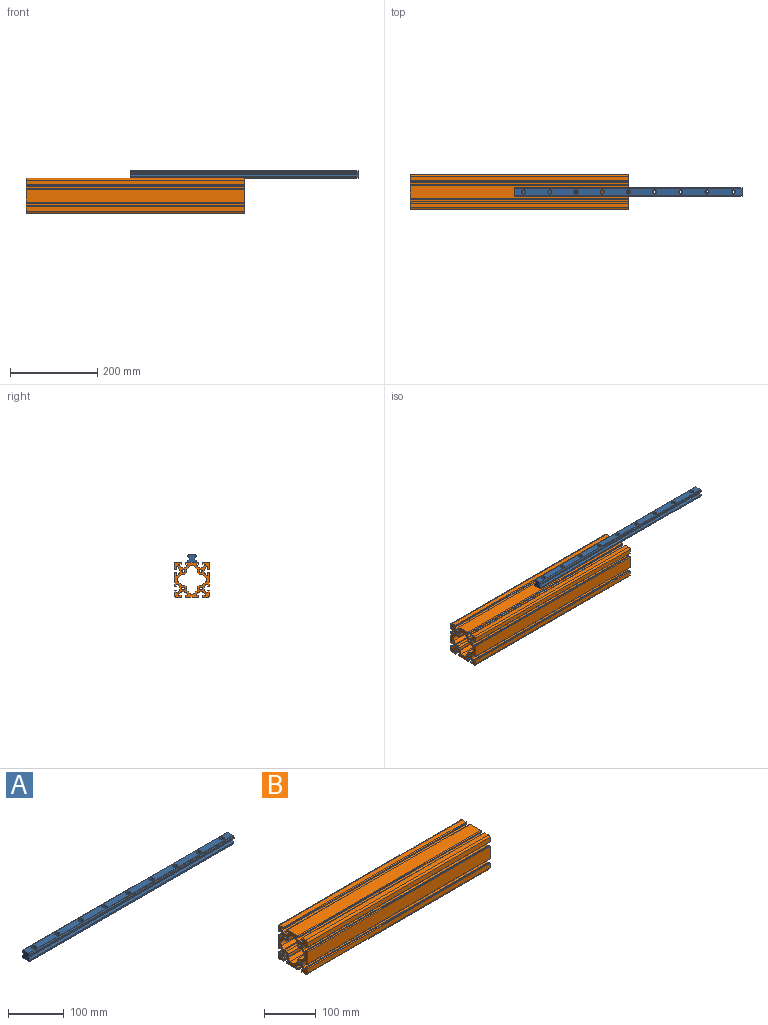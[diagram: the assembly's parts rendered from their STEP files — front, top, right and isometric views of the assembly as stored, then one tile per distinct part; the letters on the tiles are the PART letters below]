
ASSEMBLY  parts=2 mates=1
PART A: 53 faces, bbox 520x20x17.4 mm
  f0: cylinder r=3mm len=9mm, axis (0,0,1), area 169.6mm2, adj f27,f29
  f1: cylinder r=3mm len=9mm, axis (0,0,1), area 169.6mm2, adj f27,f30
  f2: cylinder r=3mm len=9mm, axis (0,0,1), area 169.6mm2, adj f27,f31
  f3: cylinder r=3mm len=9mm, axis (0,0,1), area 169.6mm2, adj f27,f32
  f4: cylinder r=3mm len=9mm, axis (0,0,1), area 169.6mm2, adj f27,f33
  f5: cylinder r=3mm len=9mm, axis (0,0,1), area 169.6mm2, adj f27,f34
  f6: cylinder r=3mm len=9mm, axis (0,0,1), area 169.6mm2, adj f27,f35
  f7: cylinder r=3mm len=9mm, axis (0,0,-1), area 169.6mm2, adj f27,f36
  f8: plane 520x3mm, normal (0,-1,0), area 1559.9mm2, adj f9,f28,f39,f41
  f9: plane 520x3.45mm, normal (0,-0.71,0.71), area 2537.2mm2, adj f8,f10,f39,f41
  f10: plane 520x2.43mm, normal (0,-1,0), area 1263.5mm2, adj f9,f11,f39,f41
  f11: plane 520x1.11mm, normal (0,-0.71,-0.71), area 815.2mm2, adj f10,f12,f39,f41
  f12: cylinder r=2.13mm len=520mm, axis (1,0,0), area 1543.6mm2, adj f11,f13,f39,f41
  f13: plane 520x0.41mm, normal (0,-0.71,-0.71), area 300.2mm2, adj f12,f14,f39,f41
  f14: plane 520x1.33mm, normal (0,-1,0), area 691.6mm2, adj f13,f15,f39,f41
  f15: plane 520x0.42mm, normal (0,-0.71,0.71), area 308.2mm2, adj f14,f16,f39,f41
  f16: cylinder r=2.13mm len=520mm, axis (1,0,0), area 1532.3mm2, adj f15,f38,f39,f41
  f17: cylinder r=2.13mm len=520mm, axis (1,0,0), area 1532.3mm2, adj f18,f39,f40,f41
  f18: plane 520x0.42mm, normal (0,0.71,0.71), area 308.1mm2, adj f17,f19,f39,f41
  f19: plane 520x1.33mm, normal (0,1,0), area 692mm2, adj f18,f20,f39,f41
  f20: plane 520x0.41mm, normal (0,0.71,-0.71), area 299.7mm2, adj f19,f21,f39,f41
  f21: cylinder r=2.13mm len=520mm, axis (1,0,0), area 1544.6mm2, adj f20,f22,f39,f41
  f22: plane 520x1.11mm, normal (0,0.71,-0.71), area 815mm2, adj f21,f23,f39,f41
  f23: plane 520x2.43mm, normal (0,1,0), area 1263.2mm2, adj f22,f24,f39,f41
  f24: plane 520x3.45mm, normal (0,0.71,0.71), area 2537.3mm2, adj f23,f25,f39,f41
  f25: plane 520x3mm, normal (0,1,0), area 1559.9mm2, adj f24,f26,f39,f41
  f26: plane 520x1mm, normal (0,0.71,-0.71), area 735.4mm2, adj f25,f27,f39,f41
  f27: plane 520x18mm, normal (0,0,-1), area 9105.5mm2, adj f0,f1,f2,f3,f4,f5,f6,f7
  f28: plane 520x1mm, normal (0,-0.71,-0.71), area 735.4mm2, adj f8,f27,f39,f41
  f29: plane 9.5x9.5mm, normal (0,0,1), area 42.6mm2, adj f0,f42
  f30: plane 9.5x9.5mm, normal (0,0,1), area 42.6mm2, adj f1,f43
  f31: plane 9.5x9.5mm, normal (0,0,1), area 42.6mm2, adj f2,f44
  f32: plane 9.5x9.5mm, normal (0,0,1), area 42.6mm2, adj f3,f45
  f33: plane 9.5x9.5mm, normal (0,0,1), area 42.6mm2, adj f4,f46
  f34: plane 9.5x9.5mm, normal (0,0,1), area 42.6mm2, adj f5,f47
  f35: plane 9.5x9.5mm, normal (0,0,1), area 42.6mm2, adj f6,f48
  f36: plane 9.5x9.5mm, normal (0,0,1), area 42.6mm2, adj f7,f49
  f37: cylinder r=3mm len=9mm, axis (0,0,1), area 169.6mm2, adj f27,f50
  f38: plane 520x0.4mm, normal (0,-0.71,0.71), area 293.8mm2, adj f16,f39,f41,f51
  f39: plane 20x17.4mm, normal (-1,0,0), area 295.2mm2, adj f8,f9,f10,f11,f12,f13,f14,f15
  f40: plane 520x0.4mm, normal (0,0.71,0.71), area 293.8mm2, adj f17,f39,f41,f51
  f41: plane 20x17.4mm, normal (1,0,0), area 295.2mm2, adj f8,f9,f10,f11,f12,f13,f14,f15
  f42: cylinder r=4.75mm len=9.5mm, axis (0,0,1), area 250.7mm2, adj f29,f51
  f43: cylinder r=4.75mm len=9.5mm, axis (0,0,1), area 250.7mm2, adj f30,f51
  f44: cylinder r=4.75mm len=9.5mm, axis (0,0,1), area 250.7mm2, adj f31,f51
  f45: cylinder r=4.75mm len=9.5mm, axis (0,0,1), area 250.7mm2, adj f32,f51
  f46: cylinder r=4.75mm len=9.5mm, axis (0,0,1), area 250.7mm2, adj f33,f51
  f47: cylinder r=4.75mm len=9.5mm, axis (0,0,1), area 250.7mm2, adj f34,f51
  f48: cylinder r=4.75mm len=9.5mm, axis (0,0,1), area 250.7mm2, adj f35,f51
  f49: cylinder r=4.75mm len=9.5mm, axis (0,0,-1), area 250.7mm2, adj f36,f51
  f50: plane 9.5x9.5mm, normal (0,0,1), area 42.6mm2, adj f37,f52
  f51: plane 520x14.52mm, normal (0,0,1), area 6912.5mm2, adj f38,f39,f40,f41,f42,f43,f44,f45
  f52: cylinder r=4.75mm len=9.5mm, axis (0,0,1), area 250.7mm2, adj f50,f51
PART B: 174 faces, bbox 500x80x80 mm
  f0: cylinder r=25mm len=500mm, axis (1,0,0), area 3705.1mm2, adj f1,f169,f172,f173
  f1: cylinder r=4mm len=500mm, axis (1,0,0), area 1279mm2, adj f0,f2,f172,f173
  f2: plane 500x4.39mm, normal (0,-1,0), area 2193.1mm2, adj f1,f3,f172,f173
  f3: cylinder r=4mm len=500mm, axis (1,0,0), area 1279mm2, adj f2,f4,f172,f173
  f4: cylinder r=25mm len=500mm, axis (1,0,0), area 3705.1mm2, adj f3,f5,f172,f173
  f5: cylinder r=1.08mm len=500mm, axis (1,0,0), area 1195.3mm2, adj f4,f6,f172,f173
  f6: plane 500x3.92mm, normal (0,1,0), area 1958.1mm2, adj f5,f7,f172,f173
  f7: cylinder r=1mm len=500mm, axis (1,0,0), area 785.4mm2, adj f6,f8,f172,f173
  f8: plane 500x2mm, normal (0,0,1), area 1000mm2, adj f7,f9,f172,f173
  f9: cylinder r=1.5mm len=500mm, axis (1,0,0), area 1178.1mm2, adj f8,f10,f172,f173
  f10: plane 500x10.5mm, normal (0,-1,0), area 5250mm2, adj f9,f11,f172,f173
  f11: cylinder r=4mm len=500mm, axis (1,0,0), area 3141.6mm2, adj f10,f12,f172,f173
  f12: plane 500x10.5mm, normal (0,0,-1), area 5250mm2, adj f11,f13,f172,f173
  f13: cylinder r=1.5mm len=500mm, axis (1,0,0), area 1178.1mm2, adj f12,f14,f172,f173
  f14: plane 500x2mm, normal (0,1,0), area 1000mm2, adj f13,f15,f172,f173
  f15: cylinder r=1mm len=500mm, axis (1,0,0), area 785.4mm2, adj f14,f16,f172,f173
  f16: plane 500x3.92mm, normal (0,0,1), area 1958.1mm2, adj f15,f17,f172,f173
  f17: cylinder r=1.08mm len=500mm, axis (1,0,0), area 1195.3mm2, adj f16,f18,f172,f173
  f18: cylinder r=25mm len=500mm, axis (1,0,0), area 3705.1mm2, adj f17,f19,f172,f173
  f19: cylinder r=4mm len=500mm, axis (1,0,0), area 1279mm2, adj f18,f20,f172,f173
  f20: plane 500x4.39mm, normal (0,0,-1), area 2193.1mm2, adj f19,f21,f172,f173
  f21: cylinder r=4mm len=500mm, axis (1,0,0), area 1279mm2, adj f20,f22,f172,f173
  f22: cylinder r=25mm len=500mm, axis (1,0,0), area 3705.1mm2, adj f21,f23,f172,f173
  f23: cylinder r=1.08mm len=500mm, axis (1,0,0), area 1195.3mm2, adj f22,f24,f172,f173
  f24: plane 500x3.92mm, normal (0,0,1), area 1958.1mm2, adj f23,f25,f172,f173
  f25: cylinder r=1mm len=500mm, axis (1,0,0), area 785.4mm2, adj f24,f26,f172,f173
  f26: plane 500x2mm, normal (0,-1,0), area 1000mm2, adj f25,f27,f172,f173
  f27: cylinder r=1.5mm len=500mm, axis (1,0,0), area 1178.1mm2, adj f26,f28,f172,f173
  f28: plane 500x29mm, normal (0,0,-1), area 14500mm2, adj f27,f29,f172,f173
  f29: cylinder r=1.5mm len=500mm, axis (1,0,0), area 1178.1mm2, adj f28,f30,f172,f173
  f30: plane 500x2mm, normal (0,1,0), area 1000mm2, adj f29,f31,f172,f173
  f31: cylinder r=1mm len=500mm, axis (1,0,0), area 785.4mm2, adj f30,f32,f172,f173
  f32: plane 500x3.92mm, normal (0,0,1), area 1958.1mm2, adj f31,f33,f172,f173
  f33: cylinder r=1.08mm len=500mm, axis (1,0,0), area 1195.3mm2, adj f32,f34,f172,f173
  f34: cylinder r=25mm len=500mm, axis (1,0,0), area 3705.1mm2, adj f33,f35,f172,f173
  f35: cylinder r=4mm len=500mm, axis (1,0,0), area 1279mm2, adj f34,f36,f172,f173
  f36: plane 500x4.39mm, normal (0,0,-1), area 2193.1mm2, adj f35,f37,f172,f173
  f37: cylinder r=4mm len=500mm, axis (1,0,0), area 1279mm2, adj f36,f38,f172,f173
  f38: cylinder r=25mm len=500mm, axis (1,0,0), area 3705.1mm2, adj f37,f39,f172,f173
  f39: cylinder r=1.08mm len=500mm, axis (1,0,0), area 1195.3mm2, adj f38,f40,f172,f173
  f40: plane 500x3.92mm, normal (0,0,1), area 1958.1mm2, adj f39,f41,f172,f173
  f41: cylinder r=1mm len=500mm, axis (1,0,0), area 785.4mm2, adj f40,f42,f172,f173
  f42: plane 500x2mm, normal (0,-1,0), area 1000mm2, adj f41,f43,f172,f173
  f43: cylinder r=1.5mm len=500mm, axis (1,0,0), area 1178.1mm2, adj f42,f44,f172,f173
  f44: plane 500x10.5mm, normal (0,0,-1), area 5250mm2, adj f43,f45,f172,f173
  f45: cylinder r=4mm len=500mm, axis (1,0,0), area 3141.6mm2, adj f44,f46,f172,f173
  f46: plane 500x10.5mm, normal (0,1,0), area 5250mm2, adj f45,f47,f172,f173
  f47: cylinder r=1.5mm len=500mm, axis (1,0,0), area 1178.1mm2, adj f46,f48,f172,f173
  f48: plane 500x2mm, normal (0,0,1), area 1000mm2, adj f47,f49,f172,f173
  f49: cylinder r=1mm len=500mm, axis (1,0,0), area 785.4mm2, adj f48,f50,f172,f173
  f50: plane 500x3.92mm, normal (0,-1,0), area 1958.1mm2, adj f49,f51,f172,f173
  f51: cylinder r=1.08mm len=500mm, axis (1,0,0), area 1195.3mm2, adj f50,f52,f172,f173
  f52: cylinder r=25mm len=500mm, axis (1,0,0), area 3705.1mm2, adj f51,f53,f172,f173
  f53: cylinder r=4mm len=500mm, axis (1,0,0), area 1279mm2, adj f52,f54,f172,f173
  f54: plane 500x4.39mm, normal (0,1,0), area 2193.1mm2, adj f53,f55,f172,f173
  f55: cylinder r=4mm len=500mm, axis (1,0,0), area 1279mm2, adj f54,f56,f172,f173
  f56: cylinder r=25mm len=500mm, axis (1,0,0), area 3705.1mm2, adj f55,f57,f172,f173
  f57: cylinder r=1.08mm len=500mm, axis (1,0,0), area 1195.3mm2, adj f56,f58,f172,f173
  f58: plane 500x3.92mm, normal (0,-1,0), area 1958.1mm2, adj f57,f59,f172,f173
  f59: cylinder r=1mm len=500mm, axis (1,0,0), area 785.4mm2, adj f58,f60,f172,f173
  f60: plane 500x2mm, normal (0,0,-1), area 1000mm2, adj f59,f61,f172,f173
  f61: cylinder r=1.5mm len=500mm, axis (1,0,0), area 1178.1mm2, adj f60,f62,f172,f173
  f62: plane 500x29mm, normal (0,1,0), area 14500mm2, adj f61,f63,f172,f173
  f63: cylinder r=1.5mm len=500mm, axis (1,0,0), area 1178.1mm2, adj f62,f64,f172,f173
  f64: plane 500x2mm, normal (0,0,1), area 1000mm2, adj f63,f65,f172,f173
  f65: cylinder r=1mm len=500mm, axis (1,0,0), area 785.4mm2, adj f64,f66,f172,f173
  f66: plane 500x3.92mm, normal (0,-1,0), area 1958.1mm2, adj f65,f67,f172,f173
  f67: cylinder r=1.08mm len=500mm, axis (1,0,0), area 1195.3mm2, adj f66,f68,f172,f173
  f68: cylinder r=25mm len=500mm, axis (1,0,0), area 3705.1mm2, adj f67,f69,f172,f173
  f69: cylinder r=4mm len=500mm, axis (1,0,0), area 1279mm2, adj f68,f70,f172,f173
  f70: plane 500x4.39mm, normal (0,1,0), area 2193.1mm2, adj f69,f71,f172,f173
  f71: cylinder r=4mm len=500mm, axis (1,0,0), area 1279mm2, adj f70,f72,f172,f173
  f72: cylinder r=25mm len=500mm, axis (1,0,0), area 3705.1mm2, adj f71,f73,f172,f173
  f73: cylinder r=1.08mm len=500mm, axis (1,0,0), area 1195.3mm2, adj f72,f74,f172,f173
  f74: plane 500x3.92mm, normal (0,-1,0), area 1958.1mm2, adj f73,f75,f172,f173
  f75: cylinder r=1mm len=500mm, axis (1,0,0), area 785.4mm2, adj f74,f76,f172,f173
  f76: plane 500x2mm, normal (0,0,-1), area 1000mm2, adj f75,f77,f172,f173
  f77: cylinder r=1.5mm len=500mm, axis (1,0,0), area 1178.1mm2, adj f76,f78,f172,f173
  f78: plane 500x10.5mm, normal (0,1,0), area 5250mm2, adj f77,f79,f172,f173
  f79: cylinder r=4mm len=500mm, axis (1,0,0), area 3141.6mm2, adj f78,f80,f172,f173
  f80: plane 500x10.5mm, normal (0,0,1), area 5250mm2, adj f79,f81,f172,f173
  f81: cylinder r=1.5mm len=500mm, axis (1,0,0), area 1178.1mm2, adj f80,f82,f172,f173
  f82: plane 500x2mm, normal (0,-1,0), area 1000mm2, adj f81,f83,f172,f173
  f83: cylinder r=1mm len=500mm, axis (1,0,0), area 785.4mm2, adj f82,f84,f172,f173
  f84: plane 500x3.92mm, normal (0,0,-1), area 1958.1mm2, adj f83,f85,f172,f173
  f85: cylinder r=1.08mm len=500mm, axis (1,0,0), area 1195.3mm2, adj f84,f86,f172,f173
  f86: cylinder r=25mm len=500mm, axis (1,0,0), area 3705.1mm2, adj f85,f87,f172,f173
  f87: cylinder r=4mm len=500mm, axis (1,0,0), area 1279mm2, adj f86,f88,f172,f173
  f88: plane 500x4.39mm, normal (0,0,1), area 2193.1mm2, adj f87,f89,f172,f173
  f89: cylinder r=4mm len=500mm, axis (1,0,0), area 1279mm2, adj f88,f90,f172,f173
  f90: cylinder r=25mm len=500mm, axis (1,0,0), area 3705.1mm2, adj f89,f91,f172,f173
  f91: cylinder r=1.08mm len=500mm, axis (1,0,0), area 1195.3mm2, adj f90,f92,f172,f173
  f92: plane 500x3.92mm, normal (0,0,-1), area 1958.1mm2, adj f91,f93,f172,f173
  f93: cylinder r=1mm len=500mm, axis (1,0,0), area 785.4mm2, adj f92,f94,f172,f173
  f94: plane 500x2mm, normal (0,1,0), area 1000mm2, adj f93,f95,f172,f173
  f95: cylinder r=1.5mm len=500mm, axis (1,0,0), area 1178.1mm2, adj f94,f96,f172,f173
  f96: plane 500x29mm, normal (0,0,1), area 14500mm2, adj f95,f97,f172,f173
  f97: cylinder r=1.5mm len=500mm, axis (1,0,0), area 1178.1mm2, adj f96,f98,f172,f173
  f98: plane 500x2mm, normal (0,-1,0), area 1000mm2, adj f97,f99,f172,f173
  f99: cylinder r=1mm len=500mm, axis (1,0,0), area 785.4mm2, adj f98,f100,f172,f173
  f100: plane 500x3.92mm, normal (0,0,-1), area 1958.1mm2, adj f99,f101,f172,f173
  f101: cylinder r=1.08mm len=500mm, axis (1,0,0), area 1195.3mm2, adj f100,f102,f172,f173
  f102: cylinder r=25mm len=500mm, axis (1,0,0), area 3705.1mm2, adj f101,f103,f172,f173
  f103: cylinder r=4mm len=500mm, axis (1,0,0), area 1279mm2, adj f102,f104,f172,f173
  f104: plane 500x4.39mm, normal (0,0,1), area 2193.1mm2, adj f103,f105,f172,f173
  f105: cylinder r=4mm len=500mm, axis (1,0,0), area 1279mm2, adj f104,f106,f172,f173
  f106: cylinder r=25mm len=500mm, axis (1,0,0), area 3705.1mm2, adj f105,f107,f172,f173
  f107: cylinder r=1.08mm len=500mm, axis (1,0,0), area 1195.3mm2, adj f106,f108,f172,f173
  f108: plane 500x3.92mm, normal (0,0,-1), area 1958.1mm2, adj f107,f109,f172,f173
  f109: cylinder r=1mm len=500mm, axis (1,0,0), area 785.4mm2, adj f108,f110,f172,f173
  f110: plane 500x2mm, normal (0,1,0), area 1000mm2, adj f109,f111,f172,f173
  f111: cylinder r=1.5mm len=500mm, axis (1,0,0), area 1178.1mm2, adj f110,f112,f172,f173
  f112: plane 500x10.5mm, normal (0,0,1), area 5250mm2, adj f111,f113,f172,f173
  f113: cylinder r=4mm len=500mm, axis (1,0,0), area 3141.6mm2, adj f112,f114,f172,f173
  f114: plane 500x10.5mm, normal (0,-1,0), area 5250mm2, adj f113,f115,f172,f173
  f115: cylinder r=1.5mm len=500mm, axis (1,0,0), area 1178.1mm2, adj f114,f116,f172,f173
  f116: plane 500x2mm, normal (0,0,-1), area 1000mm2, adj f115,f117,f172,f173
  f117: cylinder r=1mm len=500mm, axis (1,0,0), area 785.4mm2, adj f116,f118,f172,f173
  f118: plane 500x3.92mm, normal (0,1,0), area 1958.1mm2, adj f117,f119,f172,f173
  f119: cylinder r=1.08mm len=500mm, axis (1,0,0), area 1195.3mm2, adj f118,f120,f172,f173
  f120: cylinder r=25mm len=500mm, axis (1,0,0), area 3705.1mm2, adj f119,f121,f172,f173
  f121: cylinder r=4mm len=500mm, axis (1,0,0), area 1279mm2, adj f120,f122,f172,f173
  f122: plane 500x4.39mm, normal (0,-1,0), area 2193.1mm2, adj f121,f123,f172,f173
  f123: cylinder r=4mm len=500mm, axis (1,0,0), area 1279mm2, adj f122,f124,f172,f173
  f124: cylinder r=25mm len=500mm, axis (1,0,0), area 3705.1mm2, adj f123,f125,f172,f173
  f125: cylinder r=1.08mm len=500mm, axis (1,0,0), area 1195.3mm2, adj f124,f126,f172,f173
  f126: plane 500x3.92mm, normal (0,1,0), area 1958.1mm2, adj f125,f127,f172,f173
  f127: cylinder r=1mm len=500mm, axis (1,0,0), area 785.4mm2, adj f126,f128,f172,f173
  f128: plane 500x2mm, normal (0,0,1), area 1000mm2, adj f127,f129,f172,f173
  f129: cylinder r=1.5mm len=500mm, axis (1,0,0), area 1178.1mm2, adj f128,f130,f172,f173
  f130: plane 500x29mm, normal (0,-1,0), area 14500mm2, adj f129,f131,f172,f173
  f131: cylinder r=1.5mm len=500mm, axis (1,0,0), area 1178.1mm2, adj f130,f132,f172,f173
  f132: plane 500x2mm, normal (0,0,-1), area 1000mm2, adj f131,f133,f172,f173
  f133: cylinder r=1mm len=500mm, axis (1,0,0), area 785.4mm2, adj f132,f134,f172,f173
  f134: plane 500x3.92mm, normal (0,1,0), area 1958.1mm2, adj f133,f169,f172,f173
  f135: cylinder r=1.5mm len=500mm, axis (1,0,0), area 589mm2, adj f136,f170,f172,f173
  f136: plane 500x6.15mm, normal (0,0.71,0.71), area 4351.4mm2, adj f135,f137,f172,f173
  f137: cylinder r=8mm len=500mm, axis (1,0,0), area 6283.2mm2, adj f136,f138,f172,f173
  f138: plane 500x6.15mm, normal (0,0.71,-0.71), area 4351.4mm2, adj f137,f139,f172,f173
  f139: cylinder r=1.5mm len=500mm, axis (1,0,0), area 589mm2, adj f138,f140,f172,f173
  f140: plane 500x7.21mm, normal (0,0,-1), area 3606mm2, adj f139,f141,f172,f173
  f141: plane 500x3.78mm, normal (0,0.71,-0.71), area 2675.9mm2, adj f140,f142,f172,f173
  f142: plane 500x7.21mm, normal (0,1,0), area 3606mm2, adj f141,f143,f172,f173
  f143: cylinder r=1.5mm len=500mm, axis (1,0,0), area 589mm2, adj f142,f144,f172,f173
  f144: plane 500x6.15mm, normal (0,0.71,-0.71), area 4351.4mm2, adj f143,f145,f172,f173
  f145: cylinder r=8mm len=500mm, axis (1,0,0), area 6283.2mm2, adj f144,f146,f172,f173
  f146: plane 500x6.15mm, normal (0,-0.71,-0.71), area 4351.4mm2, adj f145,f147,f172,f173
  f147: cylinder r=1.5mm len=500mm, axis (1,0,0), area 589mm2, adj f146,f148,f172,f173
  f148: plane 500x7.21mm, normal (0,-1,0), area 3606mm2, adj f147,f149,f172,f173
  f149: plane 500x3.78mm, normal (0,-0.71,-0.71), area 2675.9mm2, adj f148,f150,f172,f173
  f150: plane 500x7.21mm, normal (0,0,-1), area 3606mm2, adj f149,f151,f172,f173
  f151: cylinder r=1.5mm len=500mm, axis (1,0,0), area 589mm2, adj f150,f152,f172,f173
  f152: plane 500x6.15mm, normal (0,-0.71,-0.71), area 4351.4mm2, adj f151,f153,f172,f173
  f153: cylinder r=8mm len=500mm, axis (1,0,0), area 6283.2mm2, adj f152,f154,f172,f173
  f154: plane 500x6.15mm, normal (0,-0.71,0.71), area 4351.4mm2, adj f153,f155,f172,f173
  f155: cylinder r=1.5mm len=500mm, axis (1,0,0), area 589mm2, adj f154,f156,f172,f173
  f156: plane 500x7.21mm, normal (0,0,1), area 3606mm2, adj f155,f157,f172,f173
  f157: plane 500x3.78mm, normal (0,-0.71,0.71), area 2675.9mm2, adj f156,f158,f172,f173
  f158: plane 500x7.21mm, normal (0,-1,0), area 3606mm2, adj f157,f159,f172,f173
  f159: cylinder r=1.5mm len=500mm, axis (1,0,0), area 589mm2, adj f158,f160,f172,f173
  f160: plane 500x6.15mm, normal (0,-0.71,0.71), area 4351.4mm2, adj f159,f161,f172,f173
  f161: cylinder r=8mm len=500mm, axis (1,0,0), area 6283.2mm2, adj f160,f162,f172,f173
  f162: plane 500x6.15mm, normal (0,0.71,0.71), area 4351.4mm2, adj f161,f163,f172,f173
  f163: cylinder r=1.5mm len=500mm, axis (1,0,0), area 589mm2, adj f162,f164,f172,f173
  f164: plane 500x7.21mm, normal (0,1,0), area 3606mm2, adj f163,f165,f172,f173
  f165: plane 500x3.78mm, normal (0,0.71,0.71), area 2675.9mm2, adj f164,f170,f172,f173
  f166: cylinder r=3.4mm len=500mm, axis (1,0,0), area 10681.4mm2, adj f172,f173
  f167: cylinder r=3.4mm len=500mm, axis (1,0,0), area 10681.4mm2, adj f172,f173
  f168: cylinder r=3.4mm len=500mm, axis (1,0,0), area 10681.4mm2, adj f172,f173
  f169: cylinder r=1.08mm len=500mm, axis (1,0,0), area 1195.3mm2, adj f0,f134,f172,f173
  f170: plane 500x7.21mm, normal (0,0,1), area 3606mm2, adj f135,f165,f172,f173
  f171: cylinder r=3.4mm len=500mm, axis (1,0,0), area 10681.4mm2, adj f172,f173
  f172: plane 80x80mm, normal (-1,0,0), area 2686.5mm2, adj f0,f1,f2,f3,f4,f5,f6,f7
  f173: plane 80x80mm, normal (1,0,0), area 2686.5mm2, adj f0,f1,f2,f3,f4,f5,f6,f7
PLACE A t=(-277.32,-233.34,52.72)mm
PLACE B rot(axis=(0,-0.71,0.71),180deg) t=(-537.32,-233.34,12.72)mm
MATE planar B.f130 <-> A.f3  axis (0,0,1) through (-287.32,-233.34,52.72)mm
